# Revit family: Drain_Waste-Jay R.Smith-Adjustable-3510_Series
name_source: partatom
category: Plumbing Fixtures
units: mm (PartAtom-declared; Revit-internal decimal feet)

## family parameters
Always vertical = Yes
Cut with Voids When Loaded = No
OmniClass Number = 23.70.50.21.24
OmniClass Title = Waste Water Drains
Part Type = Normal
Room Calculation Point = No
Round Connector Dimension = Use Radius
Shared = No
Work Plane-Based = Yes

## types (9) — shared parameters
Assembly Code = D2030300
Backwater Valve -V = No
Ball Float Backwater Valve -BFV = No
CW Connection = No
Default Elevation = 0"
Description = Waste Drain w/ Adjustable Strainer Heads
Diameter = 9"
Finish = Metal-JayR.Smith-Cast_Iron-Duco_Coated
HW Connection = No
Installation Type = Floor Mounted
L - Speedi-Set Service Weight - 02"(50), 03"(75) & 04"(100) sizes only = No
LXH - Speedi-Set Extra Heavy - 02"(50), 03"(75) & 04"(100) sizes only = No
Manufacturer = Jay R. Smith
Material = Metal-JayR.Smith-Cast_Iron-Duco_Coated
Model = 3510
Product Documentation Link = https://www.jrsmith.com
Product Page URL = https://www.jrsmith.com
Sediment Bucket -B = No
Strainer Heads = Strainer_Heads-Jay R.Smith-Adjustable : -F10
Trap Primer Connection -P050   1/2" (13) & -P075 3/4" (19) = No
URL = http://www.jrsmith.com
Vandal Proof Grate -U = No
Vent Connection = No
Waste Connection = Yes

## per-type parameters (varying)
| type | B Height | Collar Position (1-1/4" Min to 2-1/4" Max) | Connection Type | Outlet Diameter | Outlet Radius | Trap Primer Connection (1/2" or 3/4") | Trap Primer Radius |
| 3510C02 | 4" | 1 1/4" | 2" Caulk Outlet Connection | 2" | 1" | 1/2" | 1/4" |
| 3510C03 | 4" | 1 5/8" | 3" Caulk Outlet Connection | 3" | 1 1/2" | 0" | 0" |
| 3510C04 | 4" | 1 5/8" | 4" Caulk Outlet Connection | 4" | 2" | 0" | 0" |
| 3510T02 | 3" | 1 5/8" | 2" Threaded Outlet Connection | 2" | 1" | 0" | 0" |
| 3510T03 | 3" | 1 5/8" | 3" Threaded Outlet Connection | 3" | 1 1/2" | 0" | 0" |
| 3510T04 | 3" | 1 5/8" | 4" Threaded Outlet Connection | 4" | 2" | 0" | 0" |
| 3510Y02 | 4" | 1 5/8" | 2" No-Hub Connection | 2" | 1" | 0" | 0" |
| 3510Y03 | 4" | 1 5/8" | 3" No-Hub Outlet Connection | 3" | 1 1/2" | 0" | 0" |
| 3510Y04 | 4" | 1 5/8" | 4" No-Hub Outlet Connection | 4" | 2" | 0" | 0" |

## geometry (parser evidence)
native form markers: Sweep x8
no freeform markers — native parametric forms only
